# Revit family: Electronics_Desono_Biamp_Two-Way-High-Coaxial-Surface-Mount-Loudspeaker_EX-S10SUB
name_source: partatom
category: Communication Devices
units: mm (PartAtom-declared; Revit-internal decimal feet)

## family parameters
Cut with Voids When Loaded = No
Host = Face
Maintain Annotation Orientation = No
OmniClass Number = 23.85.10.11.14.14.14
Part Type = Normal
Room Calculation Point = No
Round Connector Dimension = Use Diameter
Shared = No

## types (4) — shared parameters
Compliance = ETL listed to comply with UL 1480A,CSA STD C22.2# 62368-1
Connector Description = Terminal block; 40V 200W 8Ω Nominal Impedance
Crossover / Protection = 1.48 kHz crossover, driver protection circuitry
Default Elevation = 4' - 0"
Depth = 1' - 0 1/2"
Description = Desono™ EX-S10SUB High Output 10 Surface Mount Subwoofer
Environmental Rating = IP54 per IEC 60529, IEC 60068-2-5 (Solar Radiation),IEC 60068-2-11 (Salt Mist), IEC 60068-2-42 (SO2),IEC 60068-2-60 (Chlorine)
Finish = Refer to the Technical Drawings (pages 2-3)
Height = 1' - 9"
Input Connection = Lever-actuated wire clamping 4-position terminal block with pass-through
Manufacturer = Biamp
Mounting Provisions = ClickMount pan-tilt bracket or ClickMount U-Bracket
Nominal Beamwidth (H x V) = Omnidirectional
Nominal Continuous Power Handling = 49 V  (300 W, 8 Ω)
Nominal Maximum SPL = UXO 80Hz -Peak - 118dB - Continuous 112dB; UXO125Hz - Peak - 119dB - Continuous - 113dB
Operating Environment = Indoor/Outdoor
Operating Mode = Passive, low impedance
Operating Range (-10dB) = 38 Hz to 140 Hz
Product Documentation Link = https://downloads.biamp.com
Product Page URL = https://www.biamp.com
Product data url = https://bimobject.com
Rated Continuous Voltage = 39.8 V (32 dBV)
Rated Maximum SPL = UXO 80Hz -Peak - 122dB - Continuous 110dB; UXO125Hz - Peak - 123dB - Continuous - 111dB
Recommended Amplifers = 300 W - 600 W, 8 Ω (49 V - 69 V)
Required Accessory = 35 Hz, 18 dB high-pass flter; DSP preset
Sensitivity = 89 dB (2.83 V); 89 dB (1 W, 8 Ω nominal impedance)
Transducers = LF  1 x 10 (250 mm) treated paper cone
Transformer = 70 V: 120 W, 60 W, 30 W, 15 W;  100 V: 120 W, 60 W, 30 W
URL = https://www.biamp.com
Weight = 28.22 lb
Width = 1' - 0"

## per-type parameters (varying)
| type | Bracket Material | CMX-LG | EXUB | Grill Material | Housing Material |
| EX-S10SUB-CM W | Biamp - Plastic - White | Yes | No | Biamp - Plastic - White(Grid) | Biamp - Plastic - White |
| EX-S10SUB-CM B | Biamp - Plastic - Black | Yes | No | Biamp - Plastic - Black(Grid) | Biamp - Plastic - Black |
| EX-S10SUB-UB B | Biamp - Plastic - Black | No | Yes | Biamp - Plastic - Black(Grid) | Biamp - Plastic - Black |
| EX-S10SUB-UB W | Biamp - Plastic - White | No | Yes | Biamp - Plastic - White(Grid) | Biamp - Plastic - White |

note: column(s) folded — value = type name in every type: Model

## geometry (parser evidence)
native form markers: Sweep x10
no freeform markers — native parametric forms only
